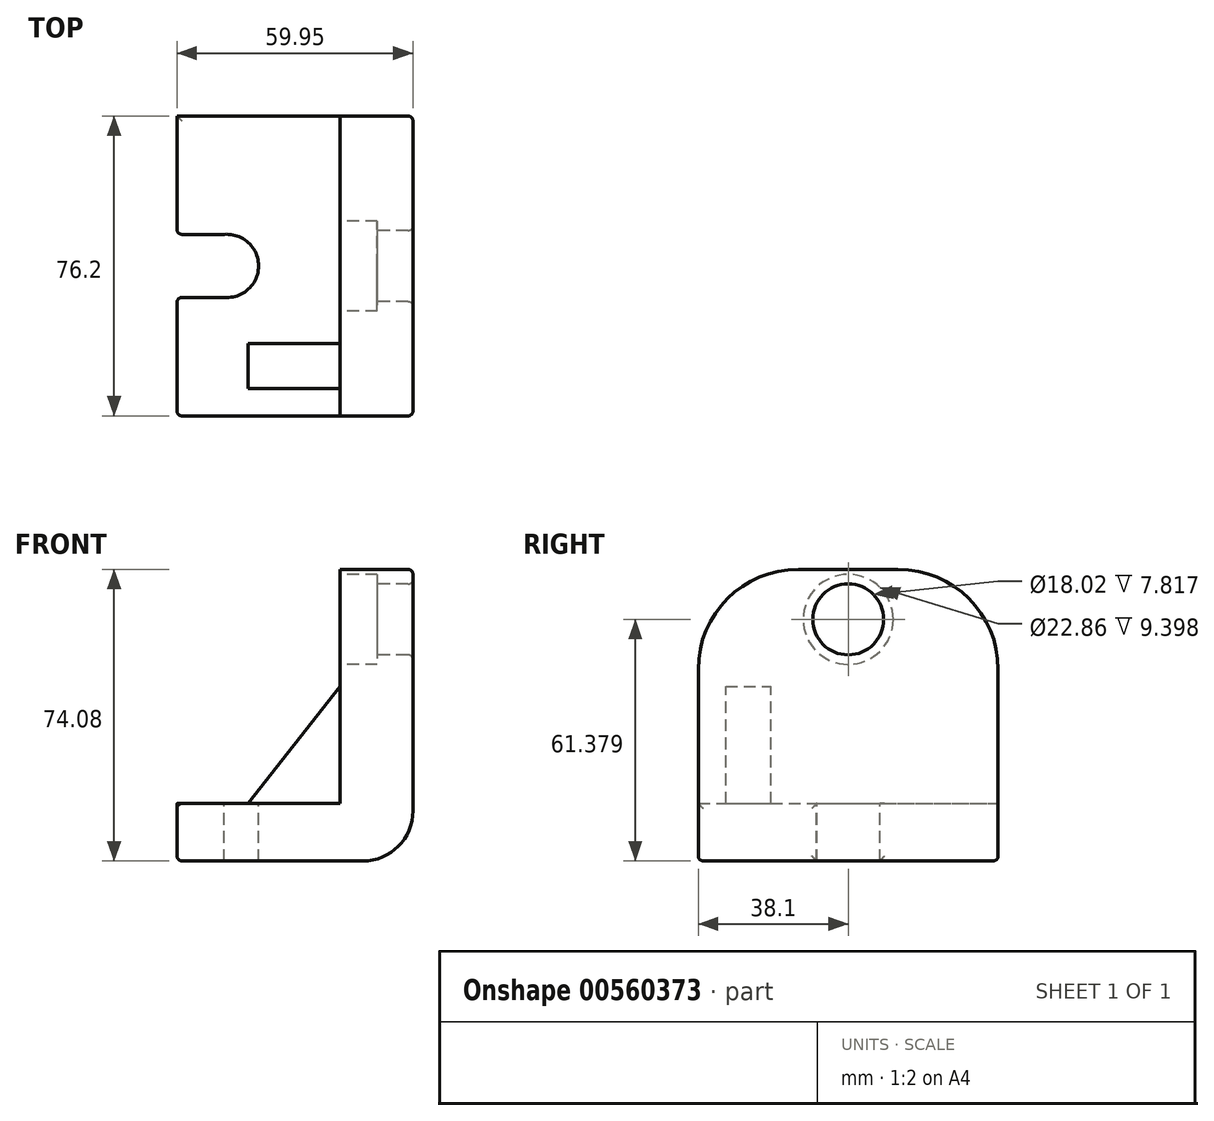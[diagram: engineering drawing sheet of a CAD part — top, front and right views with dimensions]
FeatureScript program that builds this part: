
annotation { "Feature Type Name" : "Feature", "Feature Type Description" : "" }
export const myFeature = defineFeature(function(context is Context, id is Id, definition is map)
    precondition{}
    {
        {
            var Q0;
            Q0=qCreatedBy(makeId("Front.planeOp"),FACE);
            var sketch = newSketch(context, id + "F0", { "sketchPlane" : qUnion([Q0])});
            skLineSegment(sketch, "E0", {"start": v(0, 74.08) * mm, "end": v(0, 0) * mm});
            skLineSegment(sketch, "E1", {"start": v(0, 0) * mm, "end": v(-59.95, 0) * mm});
            skLineSegment(sketch, "E2", {"start": v(-59.95, 0) * mm, "end": v(-59.95, 14.59) * mm});
            skLineSegment(sketch, "E3", {"start": v(-59.95, 14.59) * mm, "end": v(-18.49, 14.59) * mm});
            skLineSegment(sketch, "E4", {"start": v(-18.49, 14.59) * mm, "end": v(-18.49, 74.08) * mm});
            skLineSegment(sketch, "E5", {"start": v(-18.49, 74.08) * mm, "end": v(0, 74.08) * mm});
            skSolve(sketch);
        }
        {
            var Q0;
            Q0 = qSketchRegion(id + "F0", true);
            extrude(context, id + "F1", {"entities" : qUnion([Q0]), "endBound" : BoundingType.SYMMETRIC, "depth" : 76.2 * mm, "offsetDistance" : 25.4 * mm});
        }
        {
            var Q0;
            Q0=makeQuery(id+"F1.opExtrude","SWEPT_FACE",FACE,{"disambiguationData":[OSD([sQuery(id+"F0.wireOp",EDGE,"E4")])]});
            var sketch = newSketch(context, id + "F2", { "sketchPlane" : qUnion([Q0])});
            skCircle(sketch, "E6", {"center": v(0, 61.38) * mm, "radius": 9 * mm});
            skSolve(sketch);
        }
        {
            var Q0;
            Q0=makeQuery(id+"F2.imprint","IMPRINT",FACE,{"disambiguationData":[TD([[makeQuery(id+"F2.imprint","IMPRINT",EDGE,{"derivedFrom":sQuery(id+"F2.wireOp",EDGE,"E6")}),1.0]])]});
            extrude(context, id + "F3", {"entities" : qUnion([Q0]), "operationType" : NewBodyOperationType.REMOVE, "endBound" : BoundingType.UP_TO_NEXT, "oppositeDirection" : true, "depth" : 25.4 * mm, "offsetDistance" : 25.4 * mm});
        }
        {
            var Q0;
            Q0=makeQuery(id+"F1.opExtrude","SWEPT_FACE",FACE,{"disambiguationData":[OSD([sQuery(id+"F0.wireOp",EDGE,"E4")])]});
            var sketch = newSketch(context, id + "F4", { "sketchPlane" : qUnion([Q0])});
            skCircle(sketch, "E7", {"center": v(0, 61.38) * mm, "radius": 11.43 * mm});
            skSolve(sketch);
        }
        {
            var Q0;
            Q0=makeQuery(id+"F1.opExtrude","SWEPT_FACE",FACE,{"disambiguationData":[OSD([sQuery(id+"F0.wireOp",EDGE,"E3")])]});
            var sketch = newSketch(context, id + "F5", { "sketchPlane" : qUnion([Q0])});
            skCircle(sketch, "E8", {"center": v(-47.25, 0) * mm, "radius": 8.03 * mm});
            skLineSegment(sketch, "E9", {"start": v(-47.94, 8) * mm, "end": v(-59.95, 8) * mm});
            skLineSegment(sketch, "E10", {"start": v(-47.94, -8) * mm, "end": v(-59.95, -8) * mm});
            skLineSegment(sketch, "E11", {"start": v(-59.95, -8) * mm, "end": v(-59.95, 8) * mm});
            skSolve(sketch);
        }
        {
            var Q0;
            Q0=makeQuery(id+"F4.imprint","IMPRINT",FACE,{"disambiguationData":[TD([[makeQuery(id+"F4.imprint","IMPRINT",EDGE,{"derivedFrom":sQuery(id+"F4.wireOp",EDGE,"E7")}),1.0]])]});
            extrude(context, id + "F6", {"entities" : qUnion([Q0]), "operationType" : NewBodyOperationType.REMOVE, "oppositeDirection" : true, "depth" : 9.4 * mm, "offsetDistance" : 25.4 * mm});
        }
        {
            var Q0;
            {var subQ0=sQuery(id+"F5.wireOp",EDGE,"E9");Q0=makeQuery(id+"F5.imprint","IMPRINT",FACE,{"disambiguationData":[TD([[makeQuery(id+"F5.imprint","IMPRINT",EDGE,{"derivedFrom":subQ0}),1.0]])]});}
            var Q1;
            {var subQ0=sQuery(id+"F5.wireOp",EDGE,"E8");var subQ1=makeQuery(id+"F5.imprint","INTERSECT",VERTEX,{"derivedFrom":[subQ0,sQuery(id+"F5.wireOp",EDGE,"E9")]});Q1=makeQuery(id+"F5.imprint","IMPRINT",FACE,{"disambiguationData":[TD([[makeQuery(id+"F5.imprint","IMPRINT",EDGE,{"disambiguationData":[TD([[subQ1,-1.0]])],"derivedFrom":subQ0}),1.0]])]});}
            extrude(context, id + "F7", {"entities" : qUnion([Q0, Q1]), "operationType" : NewBodyOperationType.REMOVE, "oppositeDirection" : true, "depth" : 25.4 * mm, "offsetDistance" : 25.4 * mm});
        }
        {
            var Q0;
            Q0=qCreatedBy(makeId("Front.planeOp"),FACE);
            cPlane(context, id + "F8", {"entities" : qUnion([Q0]), "cplaneType" : CPlaneType.OFFSET, "offset" : 25.4 * mm, "width" : 152.4 * mm, "height" : 152.4 * mm});
        }
        {
            var Q0;
            Q0=qCreatedBy(id+"F8.planeOp",FACE);
            var sketch = newSketch(context, id + "F9", { "sketchPlane" : qUnion([Q0])});
            skLineSegment(sketch, "E12.0", {"start": v(-18.49, 14.59) * mm, "end": v(-18.49, 74.08) * mm});
            skLineSegment(sketch, "E12.1", {"start": v(-41.85, 14.59) * mm, "end": v(-18.49, 14.59) * mm});
            skLineSegment(sketch, "E13", {"start": v(-18.49, 14.59) * mm, "end": v(-18.49, 44.33) * mm});
            skLineSegment(sketch, "E14", {"start": v(-18.49, 44.33) * mm, "end": v(-41.85, 14.59) * mm});
            skSolve(sketch);
        }
        {
            var Q0;
            Q0 = qSketchRegion(id + "F9", true);
            extrude(context, id + "F10", {"entities" : qUnion([Q0]), "operationType" : NewBodyOperationType.ADD, "endBound" : BoundingType.SYMMETRIC, "depth" : 11.43 * mm, "offsetDistance" : 25.4 * mm});
        }
        {
            var Q0;
            Q0=makeQuery(id+"F1.opExtrude","SWEPT_FACE",FACE,{"disambiguationData":[OSD([sQuery(id+"F0.wireOp",EDGE,"E3")])]});
            var sketch = newSketch(context, id + "F11", { "sketchPlane" : qUnion([Q0])});
            skLineSegment(sketch, "E15.0", {"start": v(-47.94, 8) * mm, "end": v(-59.95, 8) * mm});
            skArc(sketch, "E15.1", {"start": v(-47.94, -8) * mm, "mid": v(-39.22, 0) * mm, "end": v(-47.94, 8) * mm});
            skLineSegment(sketch, "E15.2", {"start": v(-47.94, -8) * mm, "end": v(-59.95, -8) * mm});
            skLineSegment(sketch, "E16.0", {"start": v(-48.09, 11.81) * mm, "end": v(-59.95, 11.81) * mm});
            skArc(sketch, "E16.1", {"start": v(-48.09, -11.81) * mm, "mid": v(-35.4, 0) * mm, "end": v(-48.09, 11.81) * mm});
            skLineSegment(sketch, "E16.2", {"start": v(-48.09, -11.81) * mm, "end": v(-59.95, -11.81) * mm});
            skLineSegment(sketch, "E17", {"start": v(-59.95, 11.81) * mm, "end": v(-59.95, 8) * mm});
            skLineSegment(sketch, "E18", {"start": v(-59.95, -8) * mm, "end": v(-59.95, -11.81) * mm});
            skSolve(sketch);
        }
        {
            var Q0;
            Q0=makeQuery(id+"F1.opExtrude","CAP_EDGE",EDGE,{"disambiguationData":[OSD([sQuery(id+"F0.wireOp",EDGE,"E5")])],"isStart":true});
            var Q1;
            Q1=makeQuery(id+"F1.opExtrude","CAP_EDGE",EDGE,{"disambiguationData":[OSD([sQuery(id+"F0.wireOp",EDGE,"E5")])],"isStart":false});
            fillet(context, id + "F12", {"entities" : qUnion([Q0, Q1]), "radius" : 25.4 * mm, "tangentPropagation" : true, "allowEdgeOverflow" : false});
        }
        {
            var Q0;
            Q0=makeQuery(id+"F1.opExtrude","SWEPT_EDGE",EDGE,{"disambiguationData":[OSD([sQuery(id+"F0.wireOp",EDGE,"E0"),sQuery(id+"F0.wireOp",EDGE,"E1")])]});
            fillet(context, id + "F13", {"entities" : qUnion([Q0]), "radius" : 12.7 * mm, "tangentPropagation" : true, "allowEdgeOverflow" : false});
        }
        {
            var Q0;
            Q0=makeQuery(id+"F1.opExtrude","SWEPT_FACE",FACE,{"disambiguationData":[OSD([sQuery(id+"F0.wireOp",EDGE,"E0")])]});
            var Q1;
            {var subQ1=sQuery(id+"F0.wireOp",EDGE,"E2");Q1=makeQuery(id+"FOTayj9rsxtfU3l_1.boolean.opBoolean","MERGE",FACE,{"derivedFrom":[makeQuery(id+"F7.boolean.opBoolean","SPLIT",FACE,{"disambiguationData":[TD([makeQuery(id+"F7.opExtrude","SWEPT_FACE",FACE,{"disambiguationData":[OSD([sQuery(id+"F5.wireOp",EDGE,"E10")])]})])],"derivedFrom":makeQuery(id+"F1.opExtrude","SWEPT_FACE",FACE,{"disambiguationData":[OSD([subQ1])]})}),makeQuery(id+"FOTayj9rsxtfU3l_1.opExtrude","SWEPT_FACE",FACE,{"disambiguationData":[OSD([sQuery(id+"F11.wireOp",EDGE,"E18")])]})]});}
            var Q2;
            {var subQ0=sQuery(id+"F0.wireOp",EDGE,"E2");var subQ1=sQuery(id+"F0.wireOp",EDGE,"E1");Q2=makeQuery(id+"F7.boolean.opBoolean","SPLIT",EDGE,{"disambiguationData":[TD([makeQuery(id+"F7.opExtrude","SWEPT_FACE",FACE,{"disambiguationData":[OSD([sQuery(id+"F5.wireOp",EDGE,"E9")])]})])],"derivedFrom":makeQuery(id+"F1.opExtrude","SWEPT_EDGE",EDGE,{"disambiguationData":[OSD([subQ1,subQ0])]})});}
            var Q3;
            Q3=makeQuery(id+"FOTayj9rsxtfU3l_1.boolean.opBoolean","MERGE",EDGE,{"derivedFrom":[makeQuery(id+"F7.boolean.opBoolean","COPY",EDGE,{"derivedFrom":makeQuery(id+"F7.opExtrude","SWEPT_EDGE",EDGE,{"disambiguationData":[OSD([sQuery(id+"F0.wireOp",EDGE,"E2"),sQuery(id+"F0.wireOp",EDGE,"E3"),sQuery(id+"F5.wireOp",EDGE,"E9"),sQuery(id+"F5.wireOp",EDGE,"E11")])]})}),makeQuery(id+"FOTayj9rsxtfU3l_1.opExtrude","SWEPT_EDGE",EDGE,{"disambiguationData":[OSD([sQuery(id+"F11.wireOp",EDGE,"E15.0"),sQuery(id+"F11.wireOp",EDGE,"E17")])]})]});
            fillet(context, id + "F14", {"entities" : qUnion([Q0, Q1, Q2, Q3]), "radius" : 1.27 * mm, "tangentPropagation" : true, "allowEdgeOverflow" : false});
        }
    });
